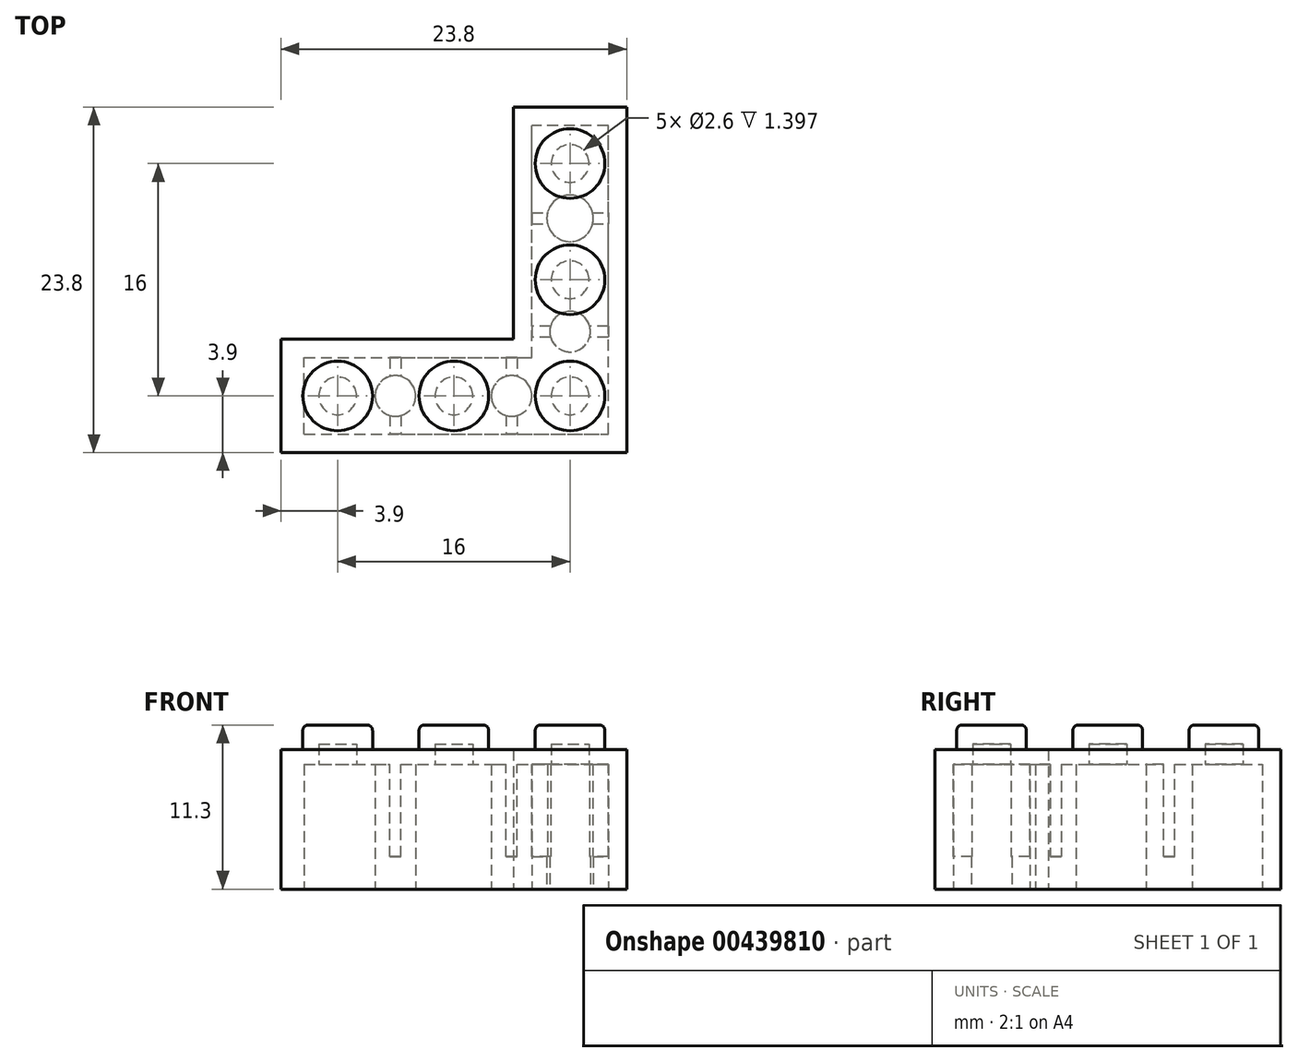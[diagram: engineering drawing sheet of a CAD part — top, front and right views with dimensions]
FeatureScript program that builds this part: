
annotation { "Feature Type Name" : "Feature", "Feature Type Description" : "" }
export const myFeature = defineFeature(function(context is Context, id is Id, definition is map)
    precondition{}
    {
        {
            var Q0;
            Q0=qCreatedBy(makeId("Top.planeOp"),FACE);
            var sketch = newSketch(context, id + "F0", { "sketchPlane" : qUnion([Q0])});
            skLineSegment(sketch, "E0.bottom", {"start": v(-16, 0) * mm, "end": v(0, 0) * mm});
            skLineSegment(sketch, "E0.top", {"start": v(-16, -7.8) * mm, "end": v(7.8, -7.8) * mm});
            skLineSegment(sketch, "E0.left", {"start": v(-16, 0) * mm, "end": v(-16, -7.8) * mm});
            skLineSegment(sketch, "E0.right", {"start": v(7.8, 0) * mm, "end": v(7.8, -7.8) * mm});
            skLineSegment(sketch, "E1.top", {"start": v(7.8, 16) * mm, "end": v(0, 16) * mm});
            skLineSegment(sketch, "E1.left", {"start": v(7.8, 0) * mm, "end": v(7.8, 16) * mm});
            skLineSegment(sketch, "E1.right", {"start": v(0, 0) * mm, "end": v(0, 16) * mm});
            skSolve(sketch);
        }
        {
            var Q0;
            Q0=makeQuery(id+"F0.imprint","IMPRINT",FACE,{"disambiguationData":[TD([[makeQuery(id+"F0.imprint","IMPRINT",EDGE,{"derivedFrom":sQuery(id+"F0.wireOp",EDGE,"E0.bottom")}),-1.0]])]});
            extrude(context, id + "F1", {"entities" : qUnion([Q0]), "depth" : 9.6 * mm});
        }
        {
            var Q0;
            Q0=makeQuery(id+"F1.opExtrude","CAP_FACE",FACE,{"disambiguationData":[OSD([sQuery(id+"F0.wireOp",EDGE,"E0.bottom"),sQuery(id+"F0.wireOp",EDGE,"E0.top"),sQuery(id+"F0.wireOp",EDGE,"E0.left"),sQuery(id+"F0.wireOp",EDGE,"E0.right"),sQuery(id+"F0.wireOp",EDGE,"E1.top"),sQuery(id+"F0.wireOp",EDGE,"E1.left"),sQuery(id+"F0.wireOp",EDGE,"E1.right")])],"isStart":false});
            var sketch = newSketch(context, id + "F2", { "sketchPlane" : qUnion([Q0])});
            skCircle(sketch, "E2", {"center": v(-12.1, -3.9) * mm, "radius": 2.4 * mm});
            skCircle(sketch, "E3", {"center": v(-4.1, -3.9) * mm, "radius": 2.4 * mm});
            skCircle(sketch, "E4", {"center": v(3.9, -3.9) * mm, "radius": 2.4 * mm});
            skCircle(sketch, "E5", {"center": v(3.9, 4.1) * mm, "radius": 2.4 * mm});
            skCircle(sketch, "E6", {"center": v(3.9, 12.1) * mm, "radius": 2.4 * mm});
            skLineSegment(sketch, "E7", {"start": v(-16, -3.9) * mm, "end": v(7.8, -3.9) * mm, "construction": true});
            skLineSegment(sketch, "E8", {"start": v(3.9, 16) * mm, "end": v(3.9, -7.8) * mm, "construction": true});
            skSolve(sketch);
        }
        {
            var Q0;
            Q0 = qSketchRegion(id + "F2", true);
            extrude(context, id + "F3", {"entities" : qUnion([Q0]), "operationType" : NewBodyOperationType.ADD, "depth" : 1.7 * mm});
        }
        {
            var Q0;
            Q0=makeQuery(id+"F3.opExtrude","CAP_EDGE",EDGE,{"disambiguationData":[OSD([sQuery(id+"F2.wireOp",EDGE,"E6")])],"isStart":false});
            var Q1;
            Q1=makeQuery(id+"F3.opExtrude","CAP_EDGE",EDGE,{"disambiguationData":[OSD([sQuery(id+"F2.wireOp",EDGE,"E5")])],"isStart":false});
            var Q2;
            Q2=makeQuery(id+"F3.opExtrude","CAP_EDGE",EDGE,{"disambiguationData":[OSD([sQuery(id+"F2.wireOp",EDGE,"E4")])],"isStart":false});
            var Q3;
            Q3=makeQuery(id+"F3.opExtrude","CAP_EDGE",EDGE,{"disambiguationData":[OSD([sQuery(id+"F2.wireOp",EDGE,"E3")])],"isStart":false});
            var Q4;
            Q4=makeQuery(id+"F3.opExtrude","CAP_EDGE",EDGE,{"disambiguationData":[OSD([sQuery(id+"F2.wireOp",EDGE,"E2")])],"isStart":false});
            fillet(context, id + "F4", {"entities" : qUnion([Q0, Q1, Q2, Q3, Q4]), "radius" : 0.38 * mm, "tangentPropagation" : true, "allowEdgeOverflow" : false});
        }
        {
            var Q0;
            Q0=makeQuery(id+"F1.opExtrude","CAP_FACE",FACE,{"disambiguationData":[OSD([sQuery(id+"F0.wireOp",EDGE,"E0.bottom"),sQuery(id+"F0.wireOp",EDGE,"E0.top"),sQuery(id+"F0.wireOp",EDGE,"E0.left"),sQuery(id+"F0.wireOp",EDGE,"E0.right"),sQuery(id+"F0.wireOp",EDGE,"E1.top"),sQuery(id+"F0.wireOp",EDGE,"E1.left"),sQuery(id+"F0.wireOp",EDGE,"E1.right")])],"isStart":true});
            var sketch = newSketch(context, id + "F5", { "sketchPlane" : qUnion([Q0])});
            skLineSegment(sketch, "E9.bottom", {"start": v(-14.4, 6.53) * mm, "end": v(6.53, 6.53) * mm});
            skLineSegment(sketch, "E9.top", {"start": v(-14.4, 1.27) * mm, "end": v(1.27, 1.27) * mm});
            skLineSegment(sketch, "E9.left", {"start": v(-14.4, 6.53) * mm, "end": v(-14.4, 1.27) * mm});
            skLineSegment(sketch, "E9.right", {"start": v(6.53, 6.53) * mm, "end": v(6.53, 1.27) * mm});
            skLineSegment(sketch, "E10.top", {"start": v(6.53, -14.73) * mm, "end": v(1.27, -14.73) * mm});
            skLineSegment(sketch, "E10.left", {"start": v(6.53, 1.27) * mm, "end": v(6.53, -14.73) * mm});
            skLineSegment(sketch, "E10.right", {"start": v(1.27, 1.27) * mm, "end": v(1.27, -14.73) * mm});
            skCircle(sketch, "E11", {"center": v(-8.13, 3.9) * mm, "radius": 1.4 * mm});
            skCircle(sketch, "E12", {"center": v(-0.12, 3.9) * mm, "radius": 1.4 * mm});
            skCircle(sketch, "E13", {"center": v(3.9, -0.53) * mm, "radius": 1.4 * mm});
            skCircle(sketch, "E14", {"center": v(3.9, -8.33) * mm, "radius": 1.6 * mm});
            skLineSegment(sketch, "E15", {"start": v(-14.4, 3.9) * mm, "end": v(6.53, 3.9) * mm, "construction": true});
            skLineSegment(sketch, "E16", {"start": v(3.9, -14.73) * mm, "end": v(3.9, 6.53) * mm, "construction": true});
            skSolve(sketch);
        }
        {
            var Q0;
            Q0=makeQuery(id+"F5.imprint","IMPRINT",FACE,{"disambiguationData":[TD([[makeQuery(id+"F5.imprint","IMPRINT",EDGE,{"derivedFrom":sQuery(id+"F5.wireOp",EDGE,"E9.bottom")}),-1.0]])]});
            extrude(context, id + "F6", {"entities" : qUnion([Q0]), "operationType" : NewBodyOperationType.REMOVE, "oppositeDirection" : true, "depth" : 8.6 * mm});
        }
        {
            var Q0;
            Q0=makeQuery(id+"F6.boolean.opBoolean","COPY",FACE,{"derivedFrom":makeQuery(id+"F6.opExtrude","CAP_FACE",FACE,{"disambiguationData":[OSD([sQuery(id+"F5.wireOp",EDGE,"E9.bottom"),sQuery(id+"F5.wireOp",EDGE,"E9.top"),sQuery(id+"F5.wireOp",EDGE,"E9.left"),sQuery(id+"F5.wireOp",EDGE,"E9.right"),sQuery(id+"F5.wireOp",EDGE,"E10.top"),sQuery(id+"F5.wireOp",EDGE,"E10.left"),sQuery(id+"F5.wireOp",EDGE,"E10.right"),sQuery(id+"F5.wireOp",EDGE,"E11"),sQuery(id+"F5.wireOp",EDGE,"E12"),sQuery(id+"F5.wireOp",EDGE,"E13"),sQuery(id+"F5.wireOp",EDGE,"E14")])],"isStart":false})});
            var sketch = newSketch(context, id + "F7", { "sketchPlane" : qUnion([Q0])});
            skCircle(sketch, "E17", {"center": v(-12.1, 3.9) * mm, "radius": 1.3 * mm});
            skCircle(sketch, "E18", {"center": v(-4.1, 3.9) * mm, "radius": 1.3 * mm});
            skCircle(sketch, "E19", {"center": v(3.9, 3.9) * mm, "radius": 1.3 * mm});
            skCircle(sketch, "E20", {"center": v(3.9, -4.1) * mm, "radius": 1.3 * mm});
            skCircle(sketch, "E21", {"center": v(3.9, -12.1) * mm, "radius": 1.3 * mm});
            skSolve(sketch);
        }
        {
            var Q0;
            Q0 = qSketchRegion(id + "F7", true);
            extrude(context, id + "F8", {"entities" : qUnion([Q0]), "operationType" : NewBodyOperationType.REMOVE, "oppositeDirection" : true, "depth" : 1.4 * mm});
        }
        {
            var Q0;
            Q0=makeQuery(id+"F6.boolean.opBoolean","COPY",FACE,{"derivedFrom":makeQuery(id+"F6.opExtrude","CAP_FACE",FACE,{"disambiguationData":[OSD([sQuery(id+"F5.wireOp",EDGE,"E9.bottom"),sQuery(id+"F5.wireOp",EDGE,"E9.top"),sQuery(id+"F5.wireOp",EDGE,"E9.left"),sQuery(id+"F5.wireOp",EDGE,"E9.right"),sQuery(id+"F5.wireOp",EDGE,"E10.top"),sQuery(id+"F5.wireOp",EDGE,"E10.left"),sQuery(id+"F5.wireOp",EDGE,"E10.right"),sQuery(id+"F5.wireOp",EDGE,"E11"),sQuery(id+"F5.wireOp",EDGE,"E12"),sQuery(id+"F5.wireOp",EDGE,"E13"),sQuery(id+"F5.wireOp",EDGE,"E14")])],"isStart":false})});
            var sketch = newSketch(context, id + "F9", { "sketchPlane" : qUnion([Q0])});
            skLineSegment(sketch, "E22", {"start": v(0.7, -8.33) * mm, "end": v(7.1, -8.33) * mm, "construction": true});
            skLineSegment(sketch, "E23", {"start": v(7.03, -0.53) * mm, "end": v(0.77, -0.53) * mm, "construction": true});
            skPoint(sketch, "E24", {"position": v(3.9, -0.53) * mm});
            skPoint(sketch, "E25", {"position": v(3.9, -8.33) * mm});
            skLineSegment(sketch, "E26.bottom", {"start": v(7.03, -0.15) * mm, "end": v(0.77, -0.15) * mm});
            skLineSegment(sketch, "E26.top", {"start": v(7.03, -0.91) * mm, "end": v(0.77, -0.91) * mm});
            skLineSegment(sketch, "E26.left", {"start": v(7.03, -0.15) * mm, "end": v(7.03, -0.91) * mm});
            skLineSegment(sketch, "E26.right", {"start": v(0.77, -0.15) * mm, "end": v(0.77, -0.91) * mm});
            skLineSegment(sketch, "E27.bottom", {"start": v(0.7, -7.95) * mm, "end": v(7.1, -7.95) * mm});
            skLineSegment(sketch, "E27.top", {"start": v(0.7, -8.7) * mm, "end": v(7.1, -8.7) * mm});
            skLineSegment(sketch, "E27.left", {"start": v(0.7, -7.95) * mm, "end": v(0.7, -8.7) * mm});
            skLineSegment(sketch, "E27.right", {"start": v(7.1, -7.95) * mm, "end": v(7.1, -8.7) * mm});
            skLineSegment(sketch, "E28.bottom", {"start": v(-7.74, 0.6) * mm, "end": v(-8.5, 0.6) * mm});
            skLineSegment(sketch, "E28.top", {"start": v(-7.74, 7.2) * mm, "end": v(-8.5, 7.2) * mm});
            skLineSegment(sketch, "E28.left", {"start": v(-7.74, 0.6) * mm, "end": v(-7.74, 7.2) * mm});
            skLineSegment(sketch, "E28.right", {"start": v(-8.5, 0.6) * mm, "end": v(-8.5, 7.2) * mm});
            skPoint(sketch, "E28.middle", {"position": v(-8.13, 3.9) * mm});
            skLineSegment(sketch, "E29.bottom", {"start": v(0.26, 0.71) * mm, "end": v(-0.5, 0.71) * mm});
            skLineSegment(sketch, "E29.top", {"start": v(0.26, 7.09) * mm, "end": v(-0.5, 7.09) * mm});
            skLineSegment(sketch, "E29.left", {"start": v(0.26, 0.71) * mm, "end": v(0.26, 7.09) * mm});
            skLineSegment(sketch, "E29.right", {"start": v(-0.5, 0.71) * mm, "end": v(-0.5, 7.09) * mm});
            skPoint(sketch, "E29.middle", {"position": v(-0.12, 3.9) * mm});
            skSolve(sketch);
        }
        {
            var Q0;
            Q0 = qSketchRegion(id + "F9", true);
            extrude(context, id + "F10", {"entities" : qUnion([Q0]), "operationType" : NewBodyOperationType.ADD, "depth" : 6.35 * mm});
        }
    });
